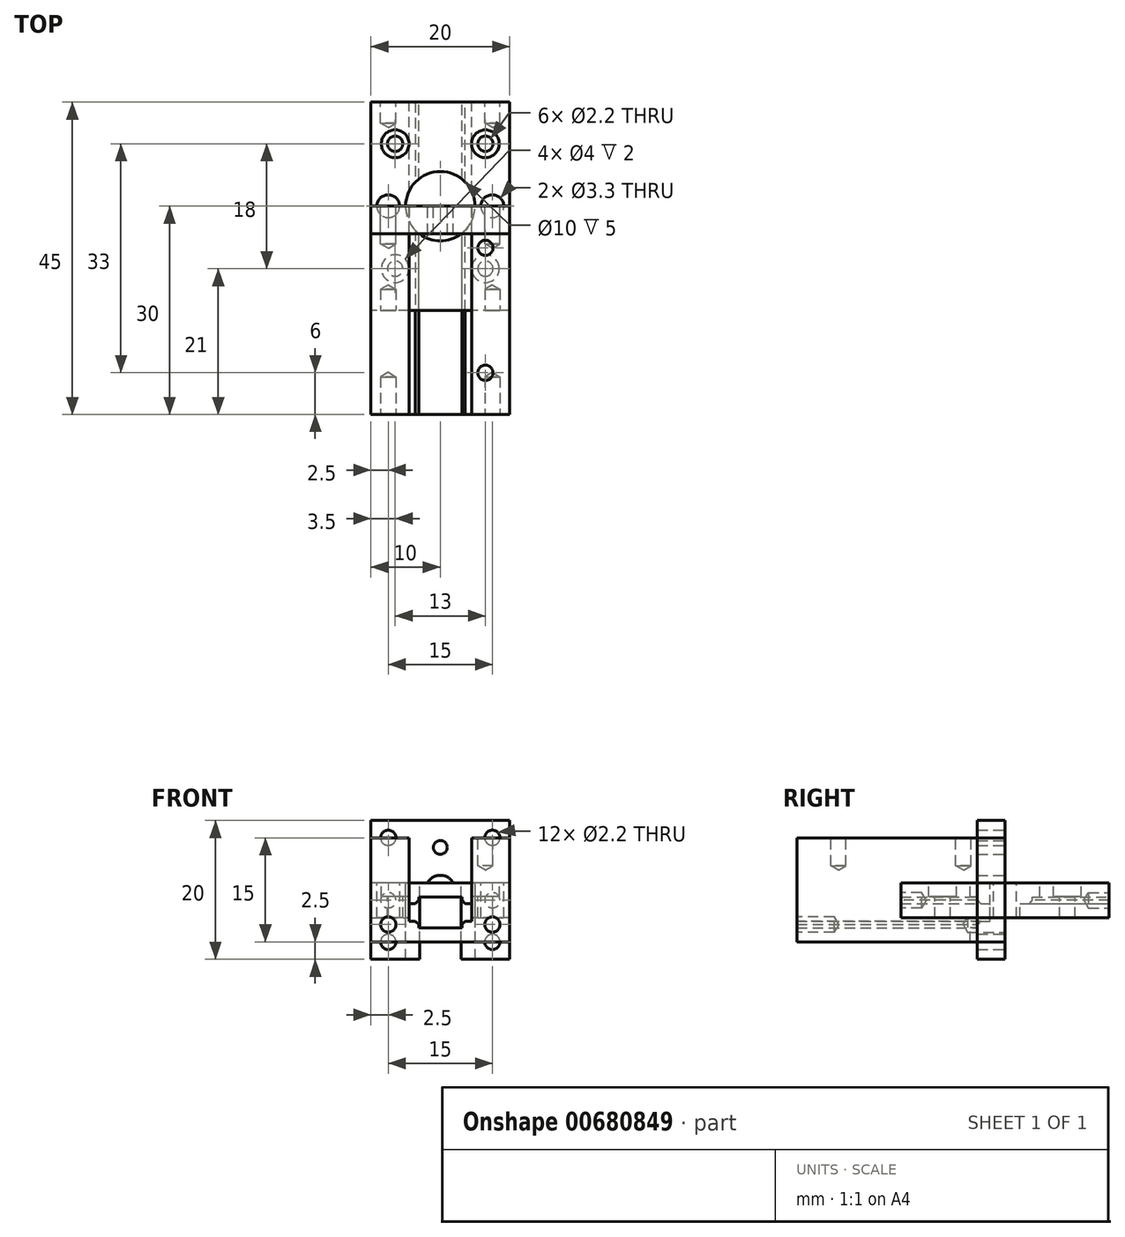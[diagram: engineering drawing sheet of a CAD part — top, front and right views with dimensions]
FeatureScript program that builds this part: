
annotation { "Feature Type Name" : "Feature", "Feature Type Description" : "" }
export const myFeature = defineFeature(function(context is Context, id is Id, definition is map)
    precondition{}
    {
        {
            var Q0;
            Q0=qCreatedBy(makeId("Front.planeOp"),FACE);
            var sketch = newSketch(context, id + "F0", { "sketchPlane" : qUnion([Q0])});
            skLineSegment(sketch, "E0.bottom", {"start": v(10, -7.5) * mm, "end": v(-10, -7.5) * mm});
            skLineSegment(sketch, "E0.top", {"start": v(10, 7.5) * mm, "end": v(4.5, 7.5) * mm});
            skPoint(sketch, "E0.middle", {"position": v(0, 0) * mm});
            skLineSegment(sketch, "E1.bottom", {"start": v(-10, 7.5) * mm, "end": v(-4.5, 7.5) * mm});
            skLineSegment(sketch, "E2.top", {"start": v(-3.1, -5.5) * mm, "end": v(3.1, -5.5) * mm});
            skLineSegment(sketch, "E3.MirrorCS", {"start": v(3.1, -4.5) * mm, "end": v(3.1, -5.5) * mm});
            skPoint(sketch, "E4.orphan", {"position": v(8, -4) * mm});
            skPoint(sketch, "E0.right.start.orphan", {"position": v(-8, -4) * mm});
            skLineSegment(sketch, "E5", {"start": v(-10, 7.5) * mm, "end": v(-10, -7.5) * mm});
            skLineSegment(sketch, "E6", {"start": v(10, -7.5) * mm, "end": v(10, 7.5) * mm});
            skLineSegment(sketch, "E7.trimOffspring", {"start": v(-4.5, 7.5) * mm, "end": v(-10, 7.5) * mm});
            skPoint(sketch, "E2.bottom.end.orphan", {"position": v(-3.1, -3.5) * mm});
            skLineSegment(sketch, "E8", {"start": v(-3.1, -5.5) * mm, "end": v(-3.1, -4.5) * mm});
            skCircle(sketch, "E9", {"center": v(-7.5, -5) * mm, "radius": 1 * mm, "construction": true});
            skCircle(sketch, "E10.MirrorC", {"center": v(7.5, -5) * mm, "radius": 1 * mm, "construction": true});
            skPoint(sketch, "E11.MirrorCS.end.orphan", {"position": v(3.1, -3.5) * mm});
            skLineSegment(sketch, "E12", {"start": v(-4.5, 7.5) * mm, "end": v(-4.5, -4.5) * mm});
            skLineSegment(sketch, "E13", {"start": v(-4.5, -4.5) * mm, "end": v(-3.1, -4.5) * mm});
            skLineSegment(sketch, "E14", {"start": v(3.1, -4.5) * mm, "end": v(4.5, -4.5) * mm});
            skLineSegment(sketch, "E15", {"start": v(4.5, 7.5) * mm, "end": v(4.5, -4.5) * mm});
            skSolve(sketch);
        }
        {
            var Q0;
            Q0=qCreatedBy(makeId("Front.planeOp"),FACE);
            var sketch = newSketch(context, id + "F1", { "sketchPlane" : qUnion([Q0])});
            skLineSegment(sketch, "E16.top", {"start": v(10, 1) * mm, "end": v(-10, 1) * mm});
            skLineSegment(sketch, "E16.left", {"start": v(10, -1) * mm, "end": v(10, 1) * mm});
            skLineSegment(sketch, "E16.right", {"start": v(-10, -3) * mm, "end": v(-10, 1) * mm});
            skPoint(sketch, "E16.middle", {"position": v(0, 0) * mm});
            skLineSegment(sketch, "E17.left", {"start": v(-3.1, -1) * mm, "end": v(-3.08, -1.02) * mm});
            skLineSegment(sketch, "E17.right", {"start": v(3.1, -1) * mm, "end": v(3.14, -1.03) * mm});
            skLineSegment(sketch, "E18.right", {"start": v(-3.1, -1) * mm, "end": v(-3.1, -2) * mm});
            skLineSegment(sketch, "E19.MirrorCS", {"start": v(3.1, -1) * mm, "end": v(3.1, -2) * mm});
            skLineSegment(sketch, "E20.trimOffspring", {"start": v(3.14, -1.03) * mm, "end": v(-3.1, -1.03) * mm});
            skLineSegment(sketch, "E21.MirrorCS", {"start": v(10, -3) * mm, "end": v(10, 1) * mm});
            skPoint(sketch, "E22.trimOffspring.end.orphan", {"position": v(-10, -1) * mm});
            skPoint(sketch, "E23.MirrorCS.end.orphan", {"position": v(6, -3) * mm});
            skLineSegment(sketch, "E24", {"start": v(-10, -3) * mm, "end": v(-10, -4) * mm});
            skLineSegment(sketch, "E25", {"start": v(-10, -4) * mm, "end": v(-4.5, -4) * mm});
            skCircle(sketch, "E26", {"center": v(-7.5, -1.5) * mm, "radius": 1 * mm, "construction": true});
            skPoint(sketch, "E27", {"position": v(-3.1, -2) * mm});
            skPoint(sketch, "E28", {"position": v(-4.5, -4) * mm});
            skLineSegment(sketch, "E29", {"start": v(-3.1, -2) * mm, "end": v(-4.5, -2) * mm});
            skLineSegment(sketch, "E30", {"start": v(-4.5, -2) * mm, "end": v(-4.5, -4) * mm});
            skLineSegment(sketch, "E31.MirrorCS", {"start": v(3.1, -2) * mm, "end": v(4.5, -2) * mm});
            skLineSegment(sketch, "E32.MirrorCS", {"start": v(4.5, -2) * mm, "end": v(4.5, -4) * mm});
            skLineSegment(sketch, "E33.MirrorCS", {"start": v(10, -4) * mm, "end": v(4.5, -4) * mm});
            skLineSegment(sketch, "E34.MirrorCS", {"start": v(10, -3) * mm, "end": v(10, -4) * mm});
            skPoint(sketch, "E35.MirrorCS.start.orphan", {"position": v(10, -3) * mm});
            skPoint(sketch, "E36", {"position": v(7.5, -1.5) * mm});
            skSolve(sketch);
        }
        {
            var Q0;
            Q0=qCreatedBy(makeId("Front.planeOp"),FACE);
            var sketch = newSketch(context, id + "F2", { "sketchPlane" : qUnion([Q0])});
            skLineSegment(sketch, "E37.bottom", {"start": v(10, -10) * mm, "end": v(-10, -10) * mm});
            skLineSegment(sketch, "E37.top", {"start": v(10, 10) * mm, "end": v(-10, 10) * mm});
            skLineSegment(sketch, "E37.left", {"start": v(10, -10) * mm, "end": v(10, 10) * mm});
            skLineSegment(sketch, "E37.right", {"start": v(-10, -10) * mm, "end": v(-10, 10) * mm});
            skPoint(sketch, "E37.middle", {"position": v(0, 0) * mm});
            skPoint(sketch, "E38", {"position": v(-7.5, 7.5) * mm});
            skPoint(sketch, "E39", {"position": v(7.5, 7.5) * mm});
            skPoint(sketch, "E40", {"position": v(-7.5, -7.5) * mm});
            skPoint(sketch, "E41", {"position": v(7.5, -7.5) * mm});
            skCircle(sketch, "E42", {"center": v(-7.5, 7.5) * mm, "radius": 2 * mm, "construction": true});
            skCircle(sketch, "E43", {"center": v(7.5, 7.5) * mm, "radius": 2 * mm, "construction": true});
            skCircle(sketch, "E44", {"center": v(-7.5, -7.5) * mm, "radius": 2 * mm, "construction": true});
            skCircle(sketch, "E45", {"center": v(7.5, -7.5) * mm, "radius": 2 * mm, "construction": true});
            skPoint(sketch, "E46", {"position": v(0, 6.11) * mm});
            skPoint(sketch, "E47", {"position": v(0, -6.11) * mm});
            skSolve(sketch);
        }
        {
            var Q0;
            Q0=makeQuery(id+"F0.imprint","IMPRINT",FACE,{"disambiguationData":[TD([[makeQuery(id+"F0.imprint","IMPRINT",EDGE,{"derivedFrom":sQuery(id+"F0.wireOp",EDGE,"E0.bottom")}),-1.0]])]});
            extrude(context, id + "F3", {"entities" : qUnion([Q0]), "depth" : 30 * mm, "offsetDistance" : 25 * mm});
        }
        {
            var Q0;
            Q0 = qSketchRegion(id + "F2", true);
            extrude(context, id + "F4", {"entities" : qUnion([Q0]), "depth" : 4 * mm, "offsetDistance" : 25 * mm});
        }
        {
            var Q0;
            Q0=sQuery(id+"F2.wireOp",VERTEX,"E38");
            var Q1;
            Q1=sQuery(id+"F2.wireOp",VERTEX,"E39");
            var Q2;
            Q2=sQuery(id+"F2.wireOp",VERTEX,"E40");
            var Q3;
            Q3=sQuery(id+"F2.wireOp",VERTEX,"E41");
            var Q4;
            Q4=makeQuery(id+"F4.opExtrude","SWEPT_BODY",BODY,{"disambiguationData":[OSD([sQuery(id+"F2.wireOp",EDGE,"E37.bottom"),sQuery(id+"F2.wireOp",EDGE,"E37.top"),sQuery(id+"F2.wireOp",EDGE,"E37.left"),sQuery(id+"F2.wireOp",EDGE,"E37.right")])]});
            hole(context, id + "F5", {"style" : HoleStyle.SIMPLE, "endStyle" : HoleEndStyle.BLIND, "oppositeDirection" : true, "holeDiameter" : 2.2 * mm, "majorDiameter" : 3 * mm, "holeDepth" : 5.4 * mm, "isTappedThrough" : true, "tappedDepth" : 3.9 * mm, "tapClearance" : 3, "locations" : qUnion([Q0, Q1, Q2, Q3]), "scope" : qUnion([Q4])});
        }
        {
            var Q0;
            Q0=sQuery(id+"F2.wireOp",VERTEX,"E46");
            var Q1;
            Q1=sQuery(id+"F2.wireOp",VERTEX,"E47");
            var Q2;
            Q2=makeQuery(id+"F4.opExtrude","SWEPT_BODY",BODY,{"disambiguationData":[OSD([sQuery(id+"F2.wireOp",EDGE,"E37.bottom"),sQuery(id+"F2.wireOp",EDGE,"E37.top"),sQuery(id+"F2.wireOp",EDGE,"E37.left"),sQuery(id+"F2.wireOp",EDGE,"E37.right")])]});
            hole(context, id + "F6", {"style" : HoleStyle.SIMPLE, "endStyle" : HoleEndStyle.BLIND, "oppositeDirection" : true, "holeDiameter" : 2 * mm, "majorDiameter" : 5 * mm, "holeDepth" : 6.3 * mm, "isTappedThrough" : true, "tappedDepth" : 3.9 * mm, "tapClearance" : 3, "locations" : qUnion([Q0, Q1]), "scope" : qUnion([Q2])});
        }
        {
            var Q0;
            Q0=sQuery(id+"F2.wireOp",VERTEX,"E37.middle");
            var Q1;
            Q1=makeQuery(id+"F4.opExtrude","SWEPT_BODY",BODY,{"disambiguationData":[OSD([sQuery(id+"F2.wireOp",EDGE,"E37.bottom"),sQuery(id+"F2.wireOp",EDGE,"E37.top"),sQuery(id+"F2.wireOp",EDGE,"E37.left"),sQuery(id+"F2.wireOp",EDGE,"E37.right")])]});
            hole(context, id + "F7", {"style" : HoleStyle.SIMPLE, "endStyle" : HoleEndStyle.BLIND, "oppositeDirection" : true, "holeDiameter" : 4.2 * mm, "majorDiameter" : 5 * mm, "holeDepth" : 5.4 * mm, "isTappedThrough" : true, "tappedDepth" : 3.9 * mm, "tapClearance" : 3, "locations" : qUnion([Q0]), "scope" : qUnion([Q1])});
        }
        {
            var Q0;
            Q0 = qSketchRegion(id + "F1", true);
            extrude(context, id + "F8", {"entities" : qUnion([Q0]), "endBound" : BoundingType.SYMMETRIC, "depth" : 30 * mm, "offsetDistance" : 25 * mm});
        }
        {
            var Q0;
            Q0=makeQuery(id+"F8.opExtrude","SWEPT_FACE",FACE,{"disambiguationData":[OSD([sQuery(id+"F1.wireOp",EDGE,"E16.top")])]});
            var sketch = newSketch(context, id + "F9", { "sketchPlane" : qUnion([Q0])});
            skCircle(sketch, "E48", {"center": v(0, 0) * mm, "radius": 5 * mm});
            skPoint(sketch, "E48.centerSnap0", {"position": v(-10, 0) * mm});
            skPoint(sketch, "E49", {"position": v(-6.96, -21.9) * mm});
            skPoint(sketch, "E50", {"position": v(-6.5, -9) * mm});
            skPoint(sketch, "E51.MirrorP", {"position": v(6.5, -9) * mm});
            skPoint(sketch, "E52.MirrorP", {"position": v(-6.5, 9) * mm});
            skPoint(sketch, "E53.MirrorP", {"position": v(6.5, 9) * mm});
            skPoint(sketch, "E54", {"position": v(-7.5, 0) * mm});
            skPoint(sketch, "E55", {"position": v(7.5, 0) * mm});
            skSolve(sketch);
        }
        {
            var Q0;
            Q0=makeQuery(id+"F9.imprint","IMPRINT",FACE,{"disambiguationData":[TD([[makeQuery(id+"F9.imprint","IMPRINT",EDGE,{"derivedFrom":sQuery(id+"F9.wireOp",EDGE,"E48")}),1.0]])]});
            extrude(context, id + "F10", {"entities" : qUnion([Q0]), "operationType" : NewBodyOperationType.REMOVE, "oppositeDirection" : true, "depth" : 25 * mm, "offsetDistance" : 25 * mm});
        }
        {
            var Q0;
            Q0=sQuery(id+"F9.wireOp",VERTEX,"E50");
            var Q1;
            Q1=sQuery(id+"F9.wireOp",VERTEX,"E52.MirrorP");
            var Q2;
            Q2=sQuery(id+"F9.wireOp",VERTEX,"E53.MirrorP");
            var Q3;
            Q3=sQuery(id+"F9.wireOp",VERTEX,"E51.MirrorP");
            var Q4;
            Q4=makeQuery(id+"F8.opExtrude","SWEPT_BODY",BODY,{"disambiguationData":[OSD([sQuery(id+"F1.wireOp",EDGE,"E16.top"),sQuery(id+"F1.wireOp",EDGE,"E16.right"),sQuery(id+"F1.wireOp",EDGE,"E18.right"),sQuery(id+"F1.wireOp",EDGE,"E19.MirrorCS"),sQuery(id+"F1.wireOp",EDGE,"E20.trimOffspring"),sQuery(id+"F1.wireOp",EDGE,"E21.MirrorCS"),sQuery(id+"F1.wireOp",EDGE,"E24"),sQuery(id+"F1.wireOp",EDGE,"E25"),sQuery(id+"F1.wireOp",EDGE,"E29"),sQuery(id+"F1.wireOp",EDGE,"E30"),sQuery(id+"F1.wireOp",EDGE,"E31.MirrorCS"),sQuery(id+"F1.wireOp",EDGE,"E32.MirrorCS"),sQuery(id+"F1.wireOp",EDGE,"E33.MirrorCS"),sQuery(id+"F1.wireOp",EDGE,"E34.MirrorCS")])]});
            hole(context, id + "F11", {"style" : HoleStyle.C_BORE, "endStyle" : HoleEndStyle.BLIND, "holeDiameter" : 2.2 * mm, "cBoreDiameter" : 4 * mm, "cBoreDepth" : 2 * mm, "majorDiameter" : 3 * mm, "holeDepth" : 5.4 * mm, "isTappedThrough" : true, "tappedDepth" : 3.9 * mm, "tapClearance" : 3, "locations" : qUnion([Q0, Q1, Q2, Q3]), "scope" : qUnion([Q4])});
        }
        {
            var Q0;
            Q0=makeQuery(id+"F8.opExtrude","CAP_FACE",FACE,{"disambiguationData":[OSD([sQuery(id+"F1.wireOp",EDGE,"E16.top"),sQuery(id+"F1.wireOp",EDGE,"E16.right"),sQuery(id+"F1.wireOp",EDGE,"E18.right"),sQuery(id+"F1.wireOp",EDGE,"E19.MirrorCS"),sQuery(id+"F1.wireOp",EDGE,"E20.trimOffspring"),sQuery(id+"F1.wireOp",EDGE,"E21.MirrorCS"),sQuery(id+"F1.wireOp",EDGE,"E24"),sQuery(id+"F1.wireOp",EDGE,"E25"),sQuery(id+"F1.wireOp",EDGE,"E29"),sQuery(id+"F1.wireOp",EDGE,"E30"),sQuery(id+"F1.wireOp",EDGE,"E31.MirrorCS"),sQuery(id+"F1.wireOp",EDGE,"E32.MirrorCS"),sQuery(id+"F1.wireOp",EDGE,"E33.MirrorCS"),sQuery(id+"F1.wireOp",EDGE,"E34.MirrorCS")])],"isStart":false});
            var sketch = newSketch(context, id + "F12", { "sketchPlane" : qUnion([Q0])});
            skPoint(sketch, "E56", {"position": v(-7.5, -1.5) * mm});
            skPoint(sketch, "E57.MirrorP", {"position": v(7.5, -1.5) * mm});
            skSolve(sketch);
        }
        {
            var Q0;
            Q0=makeQuery(id+"F3.opExtrude","CAP_FACE",FACE,{"disambiguationData":[OSD([sQuery(id+"F0.wireOp",EDGE,"E0.bottom"),sQuery(id+"F0.wireOp",EDGE,"E0.top"),sQuery(id+"F0.wireOp",EDGE,"E1.right"),sQuery(id+"F0.wireOp",EDGE,"E2.top"),sQuery(id+"F0.wireOp",EDGE,"64d8632f-4d43-4430-bbf2-ff6d00f385250.MirrorCS"),sQuery(id+"F0.wireOp",EDGE,"E3.MirrorCS"),sQuery(id+"F0.wireOp",EDGE,"E5"),sQuery(id+"F0.wireOp",EDGE,"E6"),sQuery(id+"F0.wireOp",EDGE,"E7.trimOffspring"),sQuery(id+"F0.wireOp",EDGE,"E8"),sQuery(id+"F0.wireOp",EDGE,"ZJ1krRfn-SFHT-QBQh-LZdO-vCpUZzfG7FCc"),sQuery(id+"F0.wireOp",EDGE,"t6UMZ6Am-9ff7-rIPg-ZKE5-8n0U2yJzxKFR"),sQuery(id+"F0.wireOp",EDGE,"ea787cd9-ba3c-4385-8767-a9ebd8da0a780.MirrorCS"),sQuery(id+"F0.wireOp",EDGE,"00c4b9c8-0616-444a-b1ee-6bfb384fe7390.MirrorCS")])],"isStart":false});
            var sketch = newSketch(context, id + "F13", { "sketchPlane" : qUnion([Q0])});
            skPoint(sketch, "E58", {"position": v(-7.5, -5) * mm});
            skPoint(sketch, "E59.MirrorP", {"position": v(7.5, -5) * mm});
            skSolve(sketch);
        }
        {
            var Q0;
            Q0=makeQuery(id+"F3.opExtrude","CAP_FACE",FACE,{"disambiguationData":[OSD([sQuery(id+"F0.wireOp",EDGE,"E0.bottom"),sQuery(id+"F0.wireOp",EDGE,"E0.top"),sQuery(id+"F0.wireOp",EDGE,"E2.top"),sQuery(id+"F0.wireOp",EDGE,"E3.MirrorCS"),sQuery(id+"F0.wireOp",EDGE,"E5"),sQuery(id+"F0.wireOp",EDGE,"E6"),sQuery(id+"F0.wireOp",EDGE,"E7.trimOffspring"),sQuery(id+"F0.wireOp",EDGE,"E8"),sQuery(id+"F0.wireOp",EDGE,"E12"),sQuery(id+"F0.wireOp",EDGE,"E13"),sQuery(id+"F0.wireOp",EDGE,"E14"),sQuery(id+"F0.wireOp",EDGE,"E15")])],"isStart":true});
            var sketch = newSketch(context, id + "F14", { "sketchPlane" : qUnion([Q0])});
            skPoint(sketch, "E60", {"position": v(-7.5, -5) * mm});
            skPoint(sketch, "E61.MirrorP", {"position": v(7.5, -5) * mm});
            skSolve(sketch);
        }
        {
            var Q0;
            Q0=makeQuery(id+"F8.opExtrude","CAP_FACE",FACE,{"disambiguationData":[OSD([sQuery(id+"F1.wireOp",EDGE,"E16.top"),sQuery(id+"F1.wireOp",EDGE,"E16.right"),sQuery(id+"F1.wireOp",EDGE,"E18.right"),sQuery(id+"F1.wireOp",EDGE,"E19.MirrorCS"),sQuery(id+"F1.wireOp",EDGE,"E20.trimOffspring"),sQuery(id+"F1.wireOp",EDGE,"E21.MirrorCS"),sQuery(id+"F1.wireOp",EDGE,"E24"),sQuery(id+"F1.wireOp",EDGE,"E25"),sQuery(id+"F1.wireOp",EDGE,"E29"),sQuery(id+"F1.wireOp",EDGE,"E30"),sQuery(id+"F1.wireOp",EDGE,"E31.MirrorCS"),sQuery(id+"F1.wireOp",EDGE,"E32.MirrorCS"),sQuery(id+"F1.wireOp",EDGE,"E33.MirrorCS"),sQuery(id+"F1.wireOp",EDGE,"E34.MirrorCS")])],"isStart":true});
            var sketch = newSketch(context, id + "F15", { "sketchPlane" : qUnion([Q0])});
            skPoint(sketch, "E62", {"position": v(-7.5, -1.5) * mm});
            skPoint(sketch, "E63.MirrorP", {"position": v(7.5, -1.5) * mm});
            skSolve(sketch);
        }
        {
            var Q0;
            Q0=sQuery(id+"F13.wireOp",VERTEX,"E58");
            var Q1;
            Q1=sQuery(id+"F13.wireOp",VERTEX,"E59.MirrorP");
            var Q2;
            Q2=sQuery(id+"F14.wireOp",VERTEX,"E60");
            var Q3;
            Q3=sQuery(id+"F14.wireOp",VERTEX,"E61.MirrorP");
            var Q4;
            Q4=makeQuery(id+"F3.opExtrude","SWEPT_BODY",BODY,{"disambiguationData":[OSD([sQuery(id+"F0.wireOp",EDGE,"E0.bottom"),sQuery(id+"F0.wireOp",EDGE,"E0.top"),sQuery(id+"F0.wireOp",EDGE,"E1.right"),sQuery(id+"F0.wireOp",EDGE,"E2.top"),sQuery(id+"F0.wireOp",EDGE,"64d8632f-4d43-4430-bbf2-ff6d00f385250.MirrorCS"),sQuery(id+"F0.wireOp",EDGE,"E3.MirrorCS"),sQuery(id+"F0.wireOp",EDGE,"E5"),sQuery(id+"F0.wireOp",EDGE,"E6"),sQuery(id+"F0.wireOp",EDGE,"E7.trimOffspring"),sQuery(id+"F0.wireOp",EDGE,"E8"),sQuery(id+"F0.wireOp",EDGE,"ZJ1krRfn-SFHT-QBQh-LZdO-vCpUZzfG7FCc"),sQuery(id+"F0.wireOp",EDGE,"t6UMZ6Am-9ff7-rIPg-ZKE5-8n0U2yJzxKFR"),sQuery(id+"F0.wireOp",EDGE,"ea787cd9-ba3c-4385-8767-a9ebd8da0a780.MirrorCS"),sQuery(id+"F0.wireOp",EDGE,"00c4b9c8-0616-444a-b1ee-6bfb384fe7390.MirrorCS")])]});
            hole(context, id + "F16", {"style" : HoleStyle.SIMPLE, "endStyle" : HoleEndStyle.BLIND, "holeDiameter" : 2.2 * mm, "majorDiameter" : 5 * mm, "holeDepth" : 5.4 * mm, "isTappedThrough" : true, "tappedDepth" : 3.9 * mm, "tapClearance" : 3, "locations" : qUnion([Q0, Q1, Q2, Q3]), "scope" : qUnion([Q4])});
        }
        {
            var Q0;
            Q0=sQuery(id+"F12.wireOp",VERTEX,"E57.MirrorP");
            var Q1;
            Q1=sQuery(id+"F12.wireOp",VERTEX,"E56");
            var Q2;
            Q2=sQuery(id+"F15.wireOp",VERTEX,"E62");
            var Q3;
            Q3=sQuery(id+"F15.wireOp",VERTEX,"E63.MirrorP");
            var Q4;
            Q4=makeQuery(id+"F8.opExtrude","SWEPT_BODY",BODY,{"disambiguationData":[OSD([sQuery(id+"F1.wireOp",EDGE,"E16.top"),sQuery(id+"F1.wireOp",EDGE,"E16.right"),sQuery(id+"F1.wireOp",EDGE,"E18.right"),sQuery(id+"F1.wireOp",EDGE,"E19.MirrorCS"),sQuery(id+"F1.wireOp",EDGE,"E20.trimOffspring"),sQuery(id+"F1.wireOp",EDGE,"E21.MirrorCS"),sQuery(id+"F1.wireOp",EDGE,"E24"),sQuery(id+"F1.wireOp",EDGE,"E25"),sQuery(id+"F1.wireOp",EDGE,"E29"),sQuery(id+"F1.wireOp",EDGE,"E30"),sQuery(id+"F1.wireOp",EDGE,"E31.MirrorCS"),sQuery(id+"F1.wireOp",EDGE,"E32.MirrorCS"),sQuery(id+"F1.wireOp",EDGE,"E33.MirrorCS"),sQuery(id+"F1.wireOp",EDGE,"E34.MirrorCS")])]});
            hole(context, id + "F17", {"style" : HoleStyle.SIMPLE, "endStyle" : HoleEndStyle.BLIND, "holeDiameter" : 2.2 * mm, "majorDiameter" : 5 * mm, "holeDepth" : 3 * mm, "isTappedThrough" : true, "tappedDepth" : 3.9 * mm, "tapClearance" : 3, "locations" : qUnion([Q0, Q1, Q2, Q3]), "scope" : qUnion([Q4])});
        }
        {
            var Q0;
            Q0=makeQuery(id+"F3.opExtrude","SWEPT_FACE",FACE,{"disambiguationData":[OSD([sQuery(id+"F0.wireOp",EDGE,"E7.trimOffspring")])]});
            var sketch = newSketch(context, id + "F18", { "sketchPlane" : qUnion([Q0])});
            skPoint(sketch, "E64", {"position": v(-6.5, -6) * mm});
            skPoint(sketch, "E65", {"position": v(-6.5, -24) * mm});
            skSolve(sketch);
        }
        {
            var Q0;
            Q0=makeQuery(id+"F3.opExtrude","SWEPT_FACE",FACE,{"disambiguationData":[OSD([sQuery(id+"F0.wireOp",EDGE,"E0.top")])]});
            var sketch = newSketch(context, id + "F19", { "sketchPlane" : qUnion([Q0])});
            skPoint(sketch, "E66", {"position": v(6.5, -6) * mm});
            skPoint(sketch, "E67", {"position": v(6.5, -24) * mm});
            skSolve(sketch);
        }
        {
            var Q0;
            Q0=sQuery(id+"F18.wireOp",VERTEX,"E64");
            var Q1;
            Q1=sQuery(id+"F18.wireOp",VERTEX,"E65");
            var Q2;
            Q2=sQuery(id+"F19.wireOp",VERTEX,"E66");
            var Q3;
            Q3=sQuery(id+"F19.wireOp",VERTEX,"E67");
            var Q4;
            Q4=makeQuery(id+"F3.opExtrude","SWEPT_BODY",BODY,{"disambiguationData":[OSD([sQuery(id+"F0.wireOp",EDGE,"E0.bottom"),sQuery(id+"F0.wireOp",EDGE,"E0.top"),sQuery(id+"F0.wireOp",EDGE,"E2.top"),sQuery(id+"F0.wireOp",EDGE,"E3.MirrorCS"),sQuery(id+"F0.wireOp",EDGE,"E5"),sQuery(id+"F0.wireOp",EDGE,"E6"),sQuery(id+"F0.wireOp",EDGE,"E7.trimOffspring"),sQuery(id+"F0.wireOp",EDGE,"E8"),sQuery(id+"F0.wireOp",EDGE,"E12"),sQuery(id+"F0.wireOp",EDGE,"E13"),sQuery(id+"F0.wireOp",EDGE,"E14"),sQuery(id+"F0.wireOp",EDGE,"E15")])]});
            hole(context, id + "F20", {"style" : HoleStyle.SIMPLE, "endStyle" : HoleEndStyle.BLIND, "holeDiameter" : 2.2 * mm, "majorDiameter" : 5 * mm, "holeDepth" : 4 * mm, "isTappedThrough" : true, "tappedDepth" : 3.9 * mm, "tapClearance" : 3, "locations" : qUnion([Q0, Q1, Q2, Q3]), "scope" : qUnion([Q4])});
        }
        {
            var Q0;
            Q0=sQuery(id+"F9.wireOp",VERTEX,"E54");
            var Q1;
            Q1=sQuery(id+"F9.wireOp",VERTEX,"E55");
            var Q2;
            Q2=makeQuery(id+"F8.opExtrude","SWEPT_BODY",BODY,{"disambiguationData":[OSD([sQuery(id+"F1.wireOp",EDGE,"E16.top"),sQuery(id+"F1.wireOp",EDGE,"E16.right"),sQuery(id+"F1.wireOp",EDGE,"E18.right"),sQuery(id+"F1.wireOp",EDGE,"E19.MirrorCS"),sQuery(id+"F1.wireOp",EDGE,"E20.trimOffspring"),sQuery(id+"F1.wireOp",EDGE,"E21.MirrorCS"),sQuery(id+"F1.wireOp",EDGE,"E24"),sQuery(id+"F1.wireOp",EDGE,"E25"),sQuery(id+"F1.wireOp",EDGE,"E29"),sQuery(id+"F1.wireOp",EDGE,"E30"),sQuery(id+"F1.wireOp",EDGE,"E31.MirrorCS"),sQuery(id+"F1.wireOp",EDGE,"E32.MirrorCS"),sQuery(id+"F1.wireOp",EDGE,"E33.MirrorCS"),sQuery(id+"F1.wireOp",EDGE,"E34.MirrorCS")])]});
            hole(context, id + "F21", {"style" : HoleStyle.SIMPLE, "endStyle" : HoleEndStyle.BLIND, "standardTappedOrClearance" : lookupTablePath({ "standard" : "ISO", "engagement" : "75%", "pitch" : "0.7 mm", "size" : "M4", "type" : "Tapped" }), "standardBlindInLast" : lookupTablePath({ "standard" : "ISO", "engagement" : "75%", "pitch" : "0.7 mm", "size" : "M4", "type" : "Tapped" }), "holeDiameter" : 3.3 * mm, "majorDiameter" : 4 * mm, "showTappedDepth" : true, "holeDepth" : 6 * mm, "isTappedThrough" : true, "tappedDepth" : 3.9 * mm, "tapClearance" : 3, "locations" : qUnion([Q0, Q1]), "scope" : qUnion([Q2])});
        }
        {
            var Q0;
            {var subQ0=sQuery(id+"F1.wireOp",EDGE,"E29");var subQ1=sQuery(id+"F1.wireOp",EDGE,"E18.right");Q0=makeQuery(id+"F10.boolean.opBoolean","SPLIT",EDGE,{"disambiguationData":[TD([makeQuery(id+"F8.opExtrude","CAP_FACE",FACE,{"disambiguationData":[OSD([sQuery(id+"F1.wireOp",EDGE,"E16.top"),sQuery(id+"F1.wireOp",EDGE,"E16.right"),subQ1,sQuery(id+"F1.wireOp",EDGE,"E19.MirrorCS"),sQuery(id+"F1.wireOp",EDGE,"E20.trimOffspring"),sQuery(id+"F1.wireOp",EDGE,"E21.MirrorCS"),sQuery(id+"F1.wireOp",EDGE,"E24"),sQuery(id+"F1.wireOp",EDGE,"E25"),subQ0,sQuery(id+"F1.wireOp",EDGE,"E30"),sQuery(id+"F1.wireOp",EDGE,"E31.MirrorCS"),sQuery(id+"F1.wireOp",EDGE,"E32.MirrorCS"),sQuery(id+"F1.wireOp",EDGE,"E33.MirrorCS"),sQuery(id+"F1.wireOp",EDGE,"E34.MirrorCS")])],"isStart":true})])],"derivedFrom":makeQuery(id+"F8.opExtrude","SWEPT_EDGE",EDGE,{"disambiguationData":[OSD([subQ1,subQ0])]})});}
            var Q1;
            {var subQ0=sQuery(id+"F1.wireOp",EDGE,"E31.MirrorCS");var subQ1=sQuery(id+"F1.wireOp",EDGE,"E19.MirrorCS");Q1=makeQuery(id+"F10.boolean.opBoolean","SPLIT",EDGE,{"disambiguationData":[TD([makeQuery(id+"F8.opExtrude","CAP_FACE",FACE,{"disambiguationData":[OSD([sQuery(id+"F1.wireOp",EDGE,"E16.top"),sQuery(id+"F1.wireOp",EDGE,"E16.right"),sQuery(id+"F1.wireOp",EDGE,"E18.right"),subQ1,sQuery(id+"F1.wireOp",EDGE,"E20.trimOffspring"),sQuery(id+"F1.wireOp",EDGE,"E21.MirrorCS"),sQuery(id+"F1.wireOp",EDGE,"E24"),sQuery(id+"F1.wireOp",EDGE,"E25"),sQuery(id+"F1.wireOp",EDGE,"E29"),sQuery(id+"F1.wireOp",EDGE,"E30"),subQ0,sQuery(id+"F1.wireOp",EDGE,"E32.MirrorCS"),sQuery(id+"F1.wireOp",EDGE,"E33.MirrorCS"),sQuery(id+"F1.wireOp",EDGE,"E34.MirrorCS")])],"isStart":true})])],"derivedFrom":makeQuery(id+"F8.opExtrude","SWEPT_EDGE",EDGE,{"disambiguationData":[OSD([subQ1,subQ0])]})});}
            var Q2;
            {var subQ0=sQuery(id+"F1.wireOp",EDGE,"E31.MirrorCS");var subQ1=sQuery(id+"F1.wireOp",EDGE,"E19.MirrorCS");Q2=makeQuery(id+"F10.boolean.opBoolean","SPLIT",EDGE,{"disambiguationData":[TD([makeQuery(id+"F8.opExtrude","CAP_FACE",FACE,{"disambiguationData":[OSD([sQuery(id+"F1.wireOp",EDGE,"E16.top"),sQuery(id+"F1.wireOp",EDGE,"E16.right"),sQuery(id+"F1.wireOp",EDGE,"E18.right"),subQ1,sQuery(id+"F1.wireOp",EDGE,"E20.trimOffspring"),sQuery(id+"F1.wireOp",EDGE,"E21.MirrorCS"),sQuery(id+"F1.wireOp",EDGE,"E24"),sQuery(id+"F1.wireOp",EDGE,"E25"),sQuery(id+"F1.wireOp",EDGE,"E29"),sQuery(id+"F1.wireOp",EDGE,"E30"),subQ0,sQuery(id+"F1.wireOp",EDGE,"E32.MirrorCS"),sQuery(id+"F1.wireOp",EDGE,"E33.MirrorCS"),sQuery(id+"F1.wireOp",EDGE,"E34.MirrorCS")])],"isStart":false})])],"derivedFrom":makeQuery(id+"F8.opExtrude","SWEPT_EDGE",EDGE,{"disambiguationData":[OSD([subQ1,subQ0])]})});}
            var Q3;
            {var subQ0=sQuery(id+"F1.wireOp",EDGE,"E29");var subQ1=sQuery(id+"F1.wireOp",EDGE,"E18.right");Q3=makeQuery(id+"F10.boolean.opBoolean","SPLIT",EDGE,{"disambiguationData":[TD([makeQuery(id+"F8.opExtrude","CAP_FACE",FACE,{"disambiguationData":[OSD([sQuery(id+"F1.wireOp",EDGE,"E16.top"),sQuery(id+"F1.wireOp",EDGE,"E16.right"),subQ1,sQuery(id+"F1.wireOp",EDGE,"E19.MirrorCS"),sQuery(id+"F1.wireOp",EDGE,"E20.trimOffspring"),sQuery(id+"F1.wireOp",EDGE,"E21.MirrorCS"),sQuery(id+"F1.wireOp",EDGE,"E24"),sQuery(id+"F1.wireOp",EDGE,"E25"),subQ0,sQuery(id+"F1.wireOp",EDGE,"E30"),sQuery(id+"F1.wireOp",EDGE,"E31.MirrorCS"),sQuery(id+"F1.wireOp",EDGE,"E32.MirrorCS"),sQuery(id+"F1.wireOp",EDGE,"E33.MirrorCS"),sQuery(id+"F1.wireOp",EDGE,"E34.MirrorCS")])],"isStart":false})])],"derivedFrom":makeQuery(id+"F8.opExtrude","SWEPT_EDGE",EDGE,{"disambiguationData":[OSD([subQ1,subQ0])]})});}
            var Q4;
            Q4=makeQuery(id+"F3.opExtrude","SWEPT_EDGE",EDGE,{"disambiguationData":[OSD([sQuery(id+"F0.wireOp",EDGE,"E8"),sQuery(id+"F0.wireOp",EDGE,"E13")])]});
            var Q5;
            Q5=makeQuery(id+"F3.opExtrude","SWEPT_EDGE",EDGE,{"disambiguationData":[OSD([sQuery(id+"F0.wireOp",EDGE,"E3.MirrorCS"),sQuery(id+"F0.wireOp",EDGE,"E14")])]});
            chamfer(context, id + "F22", {"entities" : qUnion([Q0, Q1, Q2, Q3, Q4, Q5]), "width" : .5 * mm, "tangentPropagation" : true});
        }
    });
